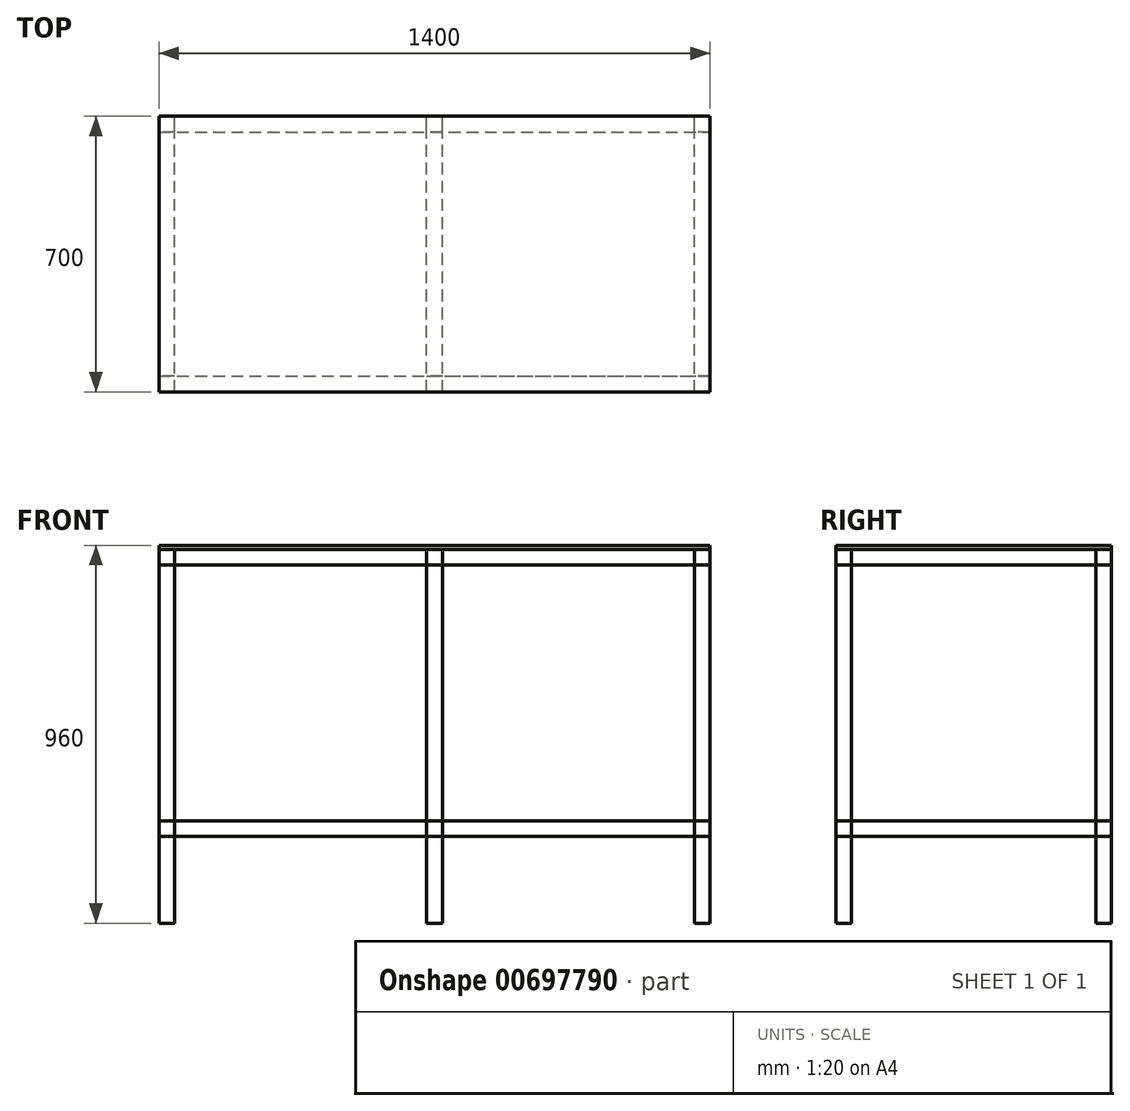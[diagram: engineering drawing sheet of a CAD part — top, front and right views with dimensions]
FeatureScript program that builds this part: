
annotation { "Feature Type Name" : "Feature", "Feature Type Description" : "" }
export const myFeature = defineFeature(function(context is Context, id is Id, definition is map)
    precondition{}
    {
        {
            var Q0;
            Q0=qCreatedBy(makeId("Top.planeOp"),FACE);
            var sketch = newSketch(context, id + "F0", { "sketchPlane" : qUnion([Q0])});
            skLineSegment(sketch, "E0.bottom", {"start": v(-1360, -40) * mm, "end": v(-1400, -40) * mm});
            skLineSegment(sketch, "E0.top", {"start": v(-1360, 0) * mm, "end": v(-1400, 0) * mm});
            skLineSegment(sketch, "E0.left", {"start": v(-1360, -40) * mm, "end": v(-1360, 0) * mm});
            skLineSegment(sketch, "E0.right", {"start": v(-1400, -40) * mm, "end": v(-1400, 0) * mm});
            skPoint(sketch, "E0.middle", {"position": v(-1380, -20) * mm});
            skLineSegment(sketch, "E1.bottom", {"start": v(-680, -40) * mm, "end": v(-720, -40) * mm});
            skLineSegment(sketch, "E1.top", {"start": v(-680, 0) * mm, "end": v(-720, 0) * mm});
            skLineSegment(sketch, "E1.left", {"start": v(-680, -40) * mm, "end": v(-680, 0) * mm});
            skLineSegment(sketch, "E1.right", {"start": v(-720, -40) * mm, "end": v(-720, 0) * mm});
            skPoint(sketch, "E1.middle", {"position": v(-700, -20) * mm});
            skLineSegment(sketch, "E2.bottom", {"start": v(-1360, -700) * mm, "end": v(-1400, -700) * mm});
            skLineSegment(sketch, "E2.top", {"start": v(-1360, -660) * mm, "end": v(-1400, -660) * mm});
            skLineSegment(sketch, "E2.left", {"start": v(-1360, -700) * mm, "end": v(-1360, -660) * mm});
            skLineSegment(sketch, "E2.right", {"start": v(-1400, -700) * mm, "end": v(-1400, -660) * mm});
            skPoint(sketch, "E2.middle", {"position": v(-1380, -680) * mm});
            skLineSegment(sketch, "E3.bottom", {"start": v(-680, -700) * mm, "end": v(-720, -700) * mm});
            skLineSegment(sketch, "E3.top", {"start": v(-680, -660) * mm, "end": v(-720, -660) * mm});
            skLineSegment(sketch, "E3.left", {"start": v(-680, -700) * mm, "end": v(-680, -660) * mm});
            skLineSegment(sketch, "E3.right", {"start": v(-720, -700) * mm, "end": v(-720, -660) * mm});
            skPoint(sketch, "E3.middle", {"position": v(-700, -680) * mm});
            skLineSegment(sketch, "E4.bottom", {"start": v(0, -700) * mm, "end": v(-40, -700) * mm});
            skLineSegment(sketch, "E4.top", {"start": v(0, -660) * mm, "end": v(-40, -660) * mm});
            skLineSegment(sketch, "E4.left", {"start": v(0, -700) * mm, "end": v(0, -660) * mm});
            skLineSegment(sketch, "E4.right", {"start": v(-40, -700) * mm, "end": v(-40, -660) * mm});
            skPoint(sketch, "E4.middle", {"position": v(-20, -680) * mm});
            skLineSegment(sketch, "E5.bottom", {"start": v(0, -40) * mm, "end": v(-40, -40) * mm});
            skLineSegment(sketch, "E5.top", {"start": v(0, 0) * mm, "end": v(-40, 0) * mm});
            skLineSegment(sketch, "E5.left", {"start": v(0, -40) * mm, "end": v(0, 0) * mm});
            skLineSegment(sketch, "E5.right", {"start": v(-40, -40) * mm, "end": v(-40, 0) * mm});
            skPoint(sketch, "E5.middle", {"position": v(-20, -20) * mm});
            skSolve(sketch);
        }
        {
            var Q0;
            Q0 = qSketchRegion(id + "F0", true);
            extrude(context, id + "F1", {"entities" : qUnion([Q0]), "depth" : 950 * mm, "offsetDistance" : 25 * mm});
        }
        {
            var Q0;
            Q0=qCreatedBy(makeId("Right.planeOp"),FACE);
            var sketch = newSketch(context, id + "F2", { "sketchPlane" : qUnion([Q0])});
            skLineSegment(sketch, "E6.bottom", {"start": v(-700, 960) * mm, "end": v(0, 960) * mm});
            skLineSegment(sketch, "E6.top", {"start": v(-700, 950) * mm, "end": v(0, 950) * mm});
            skLineSegment(sketch, "E6.left", {"start": v(-700, 960) * mm, "end": v(-700, 950) * mm});
            skLineSegment(sketch, "E6.right", {"start": v(0, 960) * mm, "end": v(0, 950) * mm});
            skLineSegment(sketch, "E7.bottom", {"start": v(-700, 260) * mm, "end": v(-660, 260) * mm});
            skLineSegment(sketch, "E7.top", {"start": v(-700, 220) * mm, "end": v(-660, 220) * mm});
            skLineSegment(sketch, "E7.left", {"start": v(-700, 260) * mm, "end": v(-700, 220) * mm});
            skLineSegment(sketch, "E7.right", {"start": v(-660, 260) * mm, "end": v(-660, 220) * mm});
            skLineSegment(sketch, "E8.bottom", {"start": v(-40, 260) * mm, "end": v(0, 260) * mm});
            skLineSegment(sketch, "E8.top", {"start": v(-40, 220) * mm, "end": v(0, 220) * mm});
            skLineSegment(sketch, "E8.left", {"start": v(-40, 260) * mm, "end": v(-40, 220) * mm});
            skLineSegment(sketch, "E8.right", {"start": v(0, 260) * mm, "end": v(0, 220) * mm});
            skSolve(sketch);
        }
        {
            var Q0;
            Q0=makeQuery(id+"F2.imprint","IMPRINT",FACE,{"disambiguationData":[TD([[makeQuery(id+"F2.imprint","IMPRINT",EDGE,{"derivedFrom":sQuery(id+"F2.wireOp",EDGE,"E7.bottom")}),-1.0]])]});
            var Q1;
            Q1=makeQuery(id+"F2.imprint","IMPRINT",FACE,{"disambiguationData":[TD([[makeQuery(id+"F2.imprint","IMPRINT",EDGE,{"derivedFrom":sQuery(id+"F2.wireOp",EDGE,"UKb49CAK-PTG1-KCDt-V7Wq-Axewzk0HyAUK.bottom")}),-1.0]])]});
            extrude(context, id + "F3", {"entities" : qUnion([Q0, Q1]), "oppositeDirection" : true, "depth" : 720 * mm, "offsetDistance" : 25 * mm});
        }
        {
            var Q0;
            Q0=makeQuery(id+"F2.imprint","IMPRINT",FACE,{"disambiguationData":[TD([[makeQuery(id+"F2.imprint","IMPRINT",EDGE,{"derivedFrom":sQuery(id+"F2.wireOp",EDGE,"E6.bottom")}),-1.0]])]});
            var Q1;
            Q1=makeQuery(id+"F2.imprint","IMPRINT",FACE,{"disambiguationData":[TD([[makeQuery(id+"F2.imprint","IMPRINT",EDGE,{"derivedFrom":sQuery(id+"F2.wireOp",EDGE,"E8.bottom")}),-1.0]])]});
            extrude(context, id + "F4", {"entities" : qUnion([Q0, Q1]), "oppositeDirection" : true, "depth" : 1400 * mm, "offsetDistance" : 25 * mm});
        }
        {
            var Q0;
            Q0=qCreatedBy(makeId("Front.planeOp"),FACE);
            var sketch = newSketch(context, id + "F5", { "sketchPlane" : qUnion([Q0])});
            skLineSegment(sketch, "E9.bottom", {"start": v(0, 260) * mm, "end": v(-40, 260) * mm});
            skLineSegment(sketch, "E9.top", {"start": v(0, 220) * mm, "end": v(-40, 220) * mm});
            skLineSegment(sketch, "E9.left", {"start": v(0, 260) * mm, "end": v(0, 220) * mm});
            skLineSegment(sketch, "E9.right", {"start": v(-40, 260) * mm, "end": v(-40, 220) * mm});
            skLineSegment(sketch, "E10.bottom", {"start": v(-680, 260) * mm, "end": v(-720, 260) * mm});
            skLineSegment(sketch, "E10.top", {"start": v(-680, 220) * mm, "end": v(-720, 220) * mm});
            skLineSegment(sketch, "E10.left", {"start": v(-680, 260) * mm, "end": v(-680, 220) * mm});
            skLineSegment(sketch, "E10.right", {"start": v(-720, 260) * mm, "end": v(-720, 220) * mm});
            skLineSegment(sketch, "E11.bottom", {"start": v(-1360, 260) * mm, "end": v(-1400, 260) * mm});
            skLineSegment(sketch, "E11.top", {"start": v(-1360, 220) * mm, "end": v(-1400, 220) * mm});
            skLineSegment(sketch, "E11.left", {"start": v(-1360, 260) * mm, "end": v(-1360, 220) * mm});
            skLineSegment(sketch, "E11.right", {"start": v(-1400, 260) * mm, "end": v(-1400, 220) * mm});
            skLineSegment(sketch, "E12.bottom", {"start": v(0, 950) * mm, "end": v(-40, 950) * mm});
            skLineSegment(sketch, "E12.top", {"start": v(0, 910) * mm, "end": v(-40, 910) * mm});
            skLineSegment(sketch, "E12.left", {"start": v(0, 950) * mm, "end": v(0, 910) * mm});
            skLineSegment(sketch, "E12.right", {"start": v(-40, 950) * mm, "end": v(-40, 910) * mm});
            skLineSegment(sketch, "E13.bottom", {"start": v(-680, 950) * mm, "end": v(-720, 950) * mm});
            skLineSegment(sketch, "E13.top", {"start": v(-680, 910) * mm, "end": v(-720, 910) * mm});
            skLineSegment(sketch, "E13.left", {"start": v(-680, 950) * mm, "end": v(-680, 910) * mm});
            skLineSegment(sketch, "E13.right", {"start": v(-720, 950) * mm, "end": v(-720, 910) * mm});
            skLineSegment(sketch, "E14.bottom", {"start": v(-1360, 950) * mm, "end": v(-1400, 950) * mm});
            skLineSegment(sketch, "E14.top", {"start": v(-1360, 910) * mm, "end": v(-1400, 910) * mm});
            skLineSegment(sketch, "E14.left", {"start": v(-1360, 950) * mm, "end": v(-1360, 910) * mm});
            skLineSegment(sketch, "E14.right", {"start": v(-1400, 950) * mm, "end": v(-1400, 910) * mm});
            skSolve(sketch);
        }
        {
            var Q0;
            Q0 = qSketchRegion(id + "F5", true);
            extrude(context, id + "F6", {"entities" : qUnion([Q0]), "depth" : 700 * mm, "offsetDistance" : 25 * mm});
        }
        {
            var Q0;
            Q0=qCreatedBy(makeId("Right.planeOp"),FACE);
            var sketch = newSketch(context, id + "F7", { "sketchPlane" : qUnion([Q0])});
            skLineSegment(sketch, "E15.bottom", {"start": v(-700, 950) * mm, "end": v(-660, 950) * mm});
            skLineSegment(sketch, "E15.top", {"start": v(-700, 910) * mm, "end": v(-660, 910) * mm});
            skLineSegment(sketch, "E15.left", {"start": v(-700, 950) * mm, "end": v(-700, 910) * mm});
            skLineSegment(sketch, "E15.right", {"start": v(-660, 950) * mm, "end": v(-660, 910) * mm});
            skLineSegment(sketch, "E16.bottom", {"start": v(-40, 950) * mm, "end": v(0, 950) * mm});
            skLineSegment(sketch, "E16.top", {"start": v(-40, 910) * mm, "end": v(0, 910) * mm});
            skLineSegment(sketch, "E16.left", {"start": v(-40, 950) * mm, "end": v(-40, 910) * mm});
            skLineSegment(sketch, "E16.right", {"start": v(0, 950) * mm, "end": v(0, 910) * mm});
            skSolve(sketch);
        }
        {
            var Q0;
            Q0=makeQuery(id+"F7.imprint","IMPRINT",FACE,{"disambiguationData":[TD([[makeQuery(id+"F7.imprint","IMPRINT",EDGE,{"derivedFrom":sQuery(id+"F7.wireOp",EDGE,"E15.bottom")}),-1.0]])]});
            var Q1;
            Q1=makeQuery(id+"F7.imprint","IMPRINT",FACE,{"disambiguationData":[TD([[makeQuery(id+"F7.imprint","IMPRINT",EDGE,{"derivedFrom":sQuery(id+"F7.wireOp",EDGE,"E16.bottom")}),-1.0]])]});
            extrude(context, id + "F8", {"entities" : qUnion([Q0, Q1]), "oppositeDirection" : true, "depth" : 1400 * mm, "offsetDistance" : 25 * mm});
        }
    });
